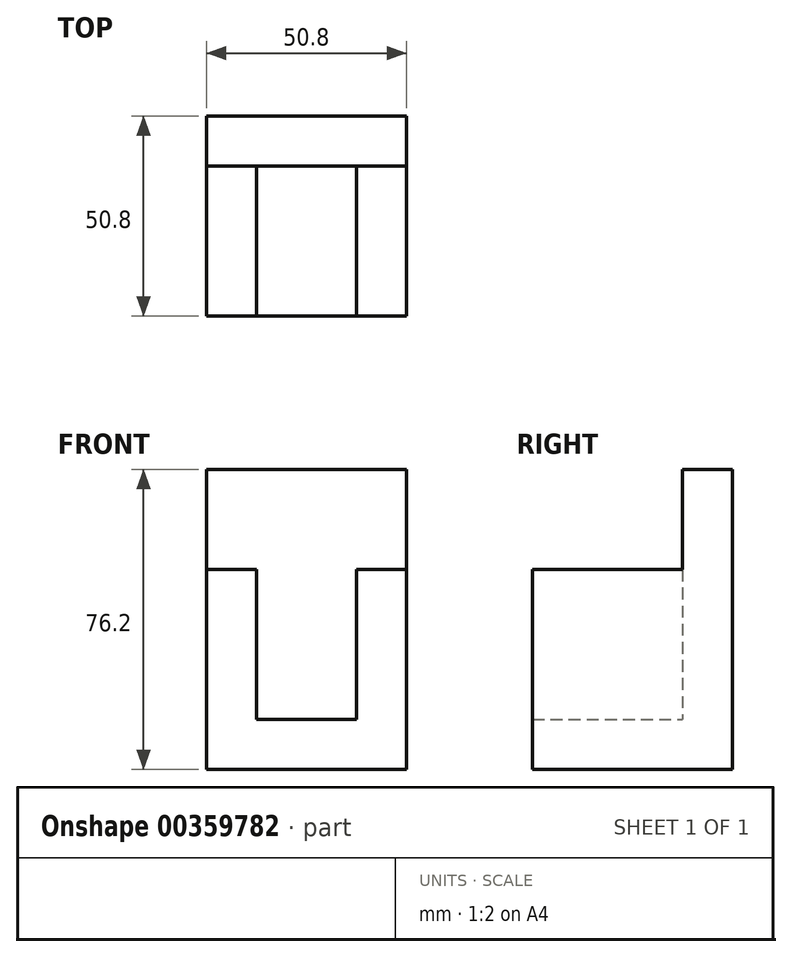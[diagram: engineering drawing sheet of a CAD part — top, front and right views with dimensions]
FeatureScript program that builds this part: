
annotation { "Feature Type Name" : "Feature", "Feature Type Description" : "" }
export const myFeature = defineFeature(function(context is Context, id is Id, definition is map)
    precondition{}
    {
        {
            var Q0;
            Q0=qCreatedBy(makeId("Front.planeOp"),FACE);
            var sketch = newSketch(context, id + "F0", { "sketchPlane" : qUnion([Q0])});
            skLineSegment(sketch, "E0.bottom", {"start": v(0, 0) * mm, "end": v(50.8, 0) * mm});
            skLineSegment(sketch, "E0.top", {"start": v(0, -76.2) * mm, "end": v(50.8, -76.2) * mm});
            skLineSegment(sketch, "E0.left", {"start": v(0, 0) * mm, "end": v(0, -76.2) * mm});
            skLineSegment(sketch, "E0.right", {"start": v(50.8, 0) * mm, "end": v(50.8, -76.2) * mm});
            skSolve(sketch);
        }
        {
            var Q0;
            Q0 = qSketchRegion(id + "F0", true);
            extrude(context, id + "F1", {"entities" : qUnion([Q0]), "depth" : 50.8 * mm});
        }
        {
            var Q0;
            Q0=makeQuery(id+"F1.opExtrude","CAP_FACE",FACE,{"disambiguationData":[OSD([sQuery(id+"F0.wireOp",EDGE,"E0.bottom"),sQuery(id+"F0.wireOp",EDGE,"E0.top"),sQuery(id+"F0.wireOp",EDGE,"E0.left"),sQuery(id+"F0.wireOp",EDGE,"E0.right")])],"isStart":false});
            var Q1;
            Q1=makeQuery(id+"F1.opExtrude","SWEPT_FACE",FACE,{"disambiguationData":[OSD([sQuery(id+"F0.wireOp",EDGE,"E0.bottom")])]});
            shell(context, id + "F2", {"entities" : qUnion([Q0, Q1]), "thickness" : 12.7 * mm});
        }
        {
            var Q0;
            Q0=makeQuery(id+"F2.opShell","OFFSET_FACE",FACE,{"disambiguationData":[OSD([sQuery(id+"F0.wireOp",EDGE,"E0.bottom"),sQuery(id+"F0.wireOp",EDGE,"E0.top"),sQuery(id+"F0.wireOp",EDGE,"E0.left"),sQuery(id+"F0.wireOp",EDGE,"E0.right")])]});
            var sketch = newSketch(context, id + "F3", { "sketchPlane" : qUnion([Q0])});
            skLineSegment(sketch, "E1.bottom", {"start": v(0, 0) * mm, "end": v(12.7, 0) * mm});
            skLineSegment(sketch, "E1.top", {"start": v(0, -25.4) * mm, "end": v(12.7, -25.4) * mm});
            skLineSegment(sketch, "E1.left", {"start": v(0, 0) * mm, "end": v(0, -25.4) * mm});
            skLineSegment(sketch, "E1.right", {"start": v(12.7, 0) * mm, "end": v(12.7, -25.4) * mm});
            skLineSegment(sketch, "E2.bottom", {"start": v(50.8, 0) * mm, "end": v(38.1, 0) * mm});
            skLineSegment(sketch, "E2.top", {"start": v(50.8, -25.4) * mm, "end": v(38.1, -25.4) * mm});
            skLineSegment(sketch, "E2.left", {"start": v(50.8, 0) * mm, "end": v(50.8, -25.4) * mm});
            skLineSegment(sketch, "E2.right", {"start": v(38.1, 0) * mm, "end": v(38.1, -25.4) * mm});
            skSolve(sketch);
        }
        {
            var Q0;
            Q0 = qSketchRegion(id + "F3", true);
            extrude(context, id + "F4", {"entities" : qUnion([Q0]), "operationType" : NewBodyOperationType.REMOVE, "depth" : 38.1 * mm});
        }
    });
